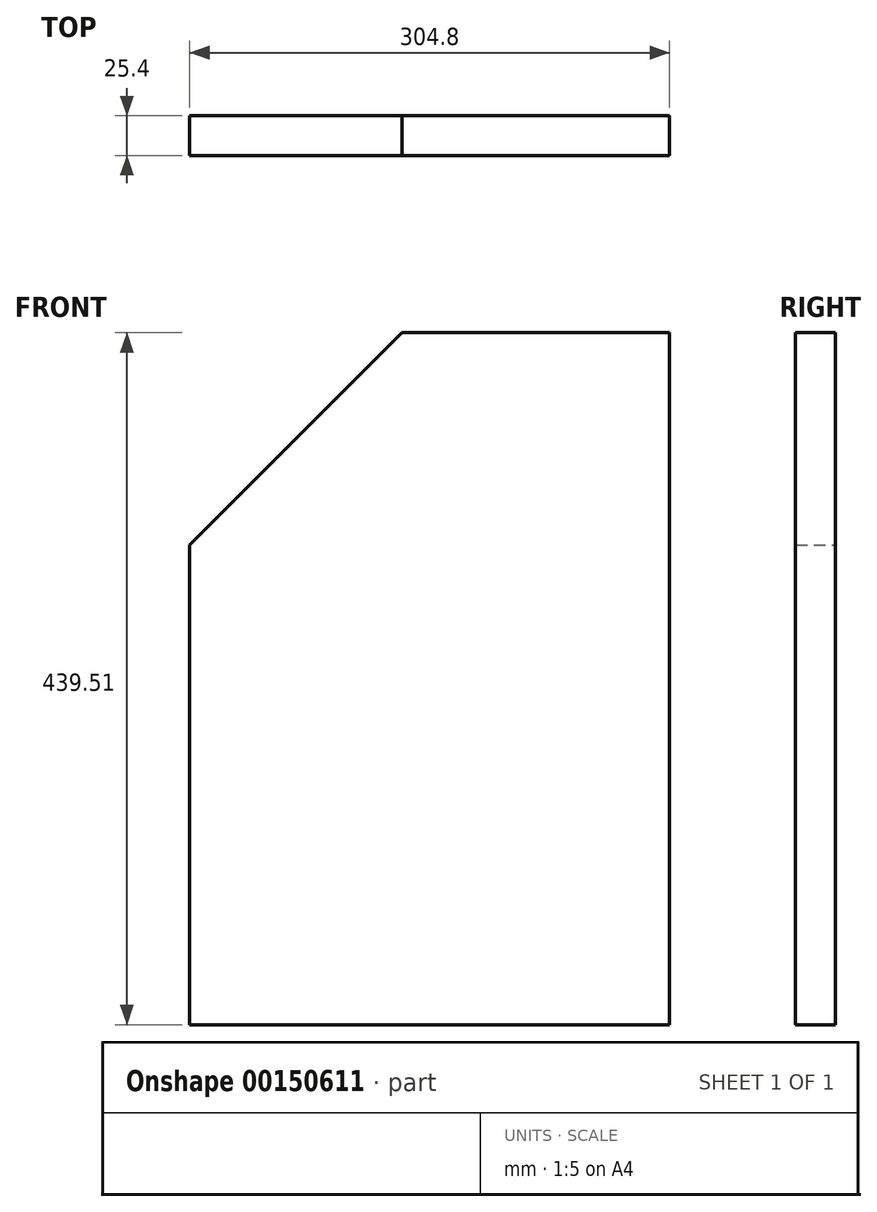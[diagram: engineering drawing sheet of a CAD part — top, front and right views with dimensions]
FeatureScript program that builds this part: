
annotation { "Feature Type Name" : "Feature", "Feature Type Description" : "" }
export const myFeature = defineFeature(function(context is Context, id is Id, definition is map)
    precondition{}
    {
        {
            var Q0;
            Q0=qCreatedBy(makeId("Front.planeOp"),FACE);
            var sketch = newSketch(context, id + "F0", { "sketchPlane" : qUnion([Q0])});
            skLineSegment(sketch, "E0", {"start": v(-35.54, -19.16) * mm, "end": v(-35.54, 285.64) * mm});
            skLineSegment(sketch, "E1", {"start": v(-35.54, 285.64) * mm, "end": v(99.16, 420.35) * mm});
            skLineSegment(sketch, "E2", {"start": v(99.16, 420.35) * mm, "end": v(269.26, 420.35) * mm});
            skLineSegment(sketch, "E3", {"start": v(-35.54, -19.16) * mm, "end": v(269.26, -19.16) * mm});
            skLineSegment(sketch, "E4", {"start": v(269.26, -19.16) * mm, "end": v(269.26, 420.35) * mm});
            skLineSegment(sketch, "E5", {"start": v(-35.54, 285.64) * mm, "end": v(269.26, 285.64) * mm});
            skSolve(sketch);
        }
        {
            var Q0;
            Q0 = qSketchRegion(id + "F0", true);
            extrude(context, id + "F1", {"entities" : qUnion([Q0]), "depth" : 25.4 * mm});
        }
    });
